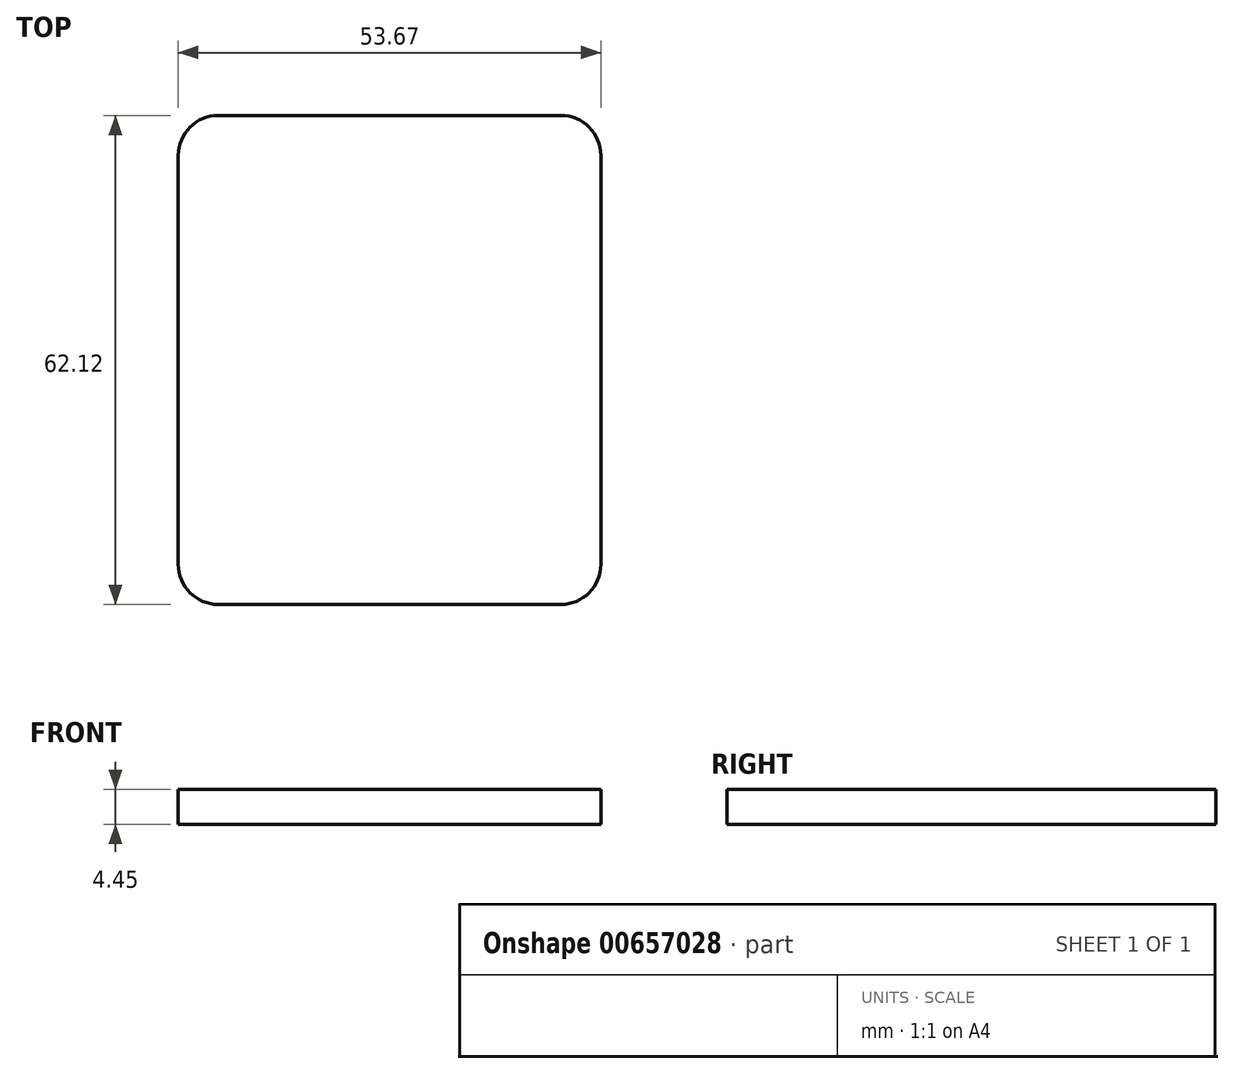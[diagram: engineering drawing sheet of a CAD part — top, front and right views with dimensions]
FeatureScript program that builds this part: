
annotation { "Feature Type Name" : "Feature", "Feature Type Description" : "" }
export const myFeature = defineFeature(function(context is Context, id is Id, definition is map)
    precondition{}
    {
        {
            var Q0;
            Q0=qCreatedBy(makeId("Top.planeOp"),FACE);
            var sketch = newSketch(context, id + "F0", { "sketchPlane" : qUnion([Q0])});
            skLineSegment(sketch, "E0.bottom", {"start": v(0, 0) * mm, "end": v(-53.67, 0) * mm});
            skLineSegment(sketch, "E0.top", {"start": v(0, 62.12) * mm, "end": v(-53.67, 62.12) * mm});
            skLineSegment(sketch, "E0.left", {"start": v(0, 0) * mm, "end": v(0, 62.12) * mm});
            skLineSegment(sketch, "E0.right", {"start": v(-53.67, 0) * mm, "end": v(-53.67, 62.12) * mm});
            skSolve(sketch);
        }
        {
            var Q0;
            Q0=makeQuery(id+"F0.imprint","IMPRINT",FACE,{"disambiguationData":[TD([[makeQuery(id+"F0.imprint","IMPRINT",EDGE,{"derivedFrom":sQuery(id+"F0.wireOp",EDGE,"E0.bottom")}),-1.0]])]});
            extrude(context, id + "F1", {"entities" : qUnion([Q0]), "depth" : 4.44 * mm, "offsetDistance" : 25.4 * mm});
        }
        {
            var Q0;
            Q0=makeQuery(id+"F1.opExtrude","SWEPT_EDGE",EDGE,{"disambiguationData":[OSD([sQuery(id+"F0.wireOp",EDGE,"E0.top"),sQuery(id+"F0.wireOp",EDGE,"E0.left")])]});
            fillet(context, id + "F2", {"entities" : qUnion([Q0]), "radius" : 5.08 * mm, "tangentPropagation" : true, "allowEdgeOverflow" : false});
        }
        {
            var Q0;
            Q0=makeQuery(id+"F1.opExtrude","SWEPT_EDGE",EDGE,{"disambiguationData":[OSD([sQuery(id+"F0.wireOp",EDGE,"E0.top"),sQuery(id+"F0.wireOp",EDGE,"E0.right")])]});
            fillet(context, id + "F3", {"entities" : qUnion([Q0]), "radius" : 5.08 * mm, "tangentPropagation" : true, "allowEdgeOverflow" : false});
        }
        {
            var Q0;
            Q0=makeQuery(id+"F1.opExtrude","SWEPT_EDGE",EDGE,{"disambiguationData":[OSD([sQuery(id+"F0.wireOp",EDGE,"E0.bottom"),sQuery(id+"F0.wireOp",EDGE,"E0.right")])]});
            fillet(context, id + "F4", {"entities" : qUnion([Q0]), "radius" : 5.08 * mm, "tangentPropagation" : true, "allowEdgeOverflow" : false});
        }
        {
            var Q0;
            Q0=makeQuery(id+"F1.opExtrude","SWEPT_EDGE",EDGE,{"disambiguationData":[OSD([sQuery(id+"F0.wireOp",EDGE,"E0.bottom"),sQuery(id+"F0.wireOp",EDGE,"E0.left")])]});
            fillet(context, id + "F5", {"entities" : qUnion([Q0]), "radius" : 5.08 * mm, "tangentPropagation" : true, "allowEdgeOverflow" : false});
        }
    });
